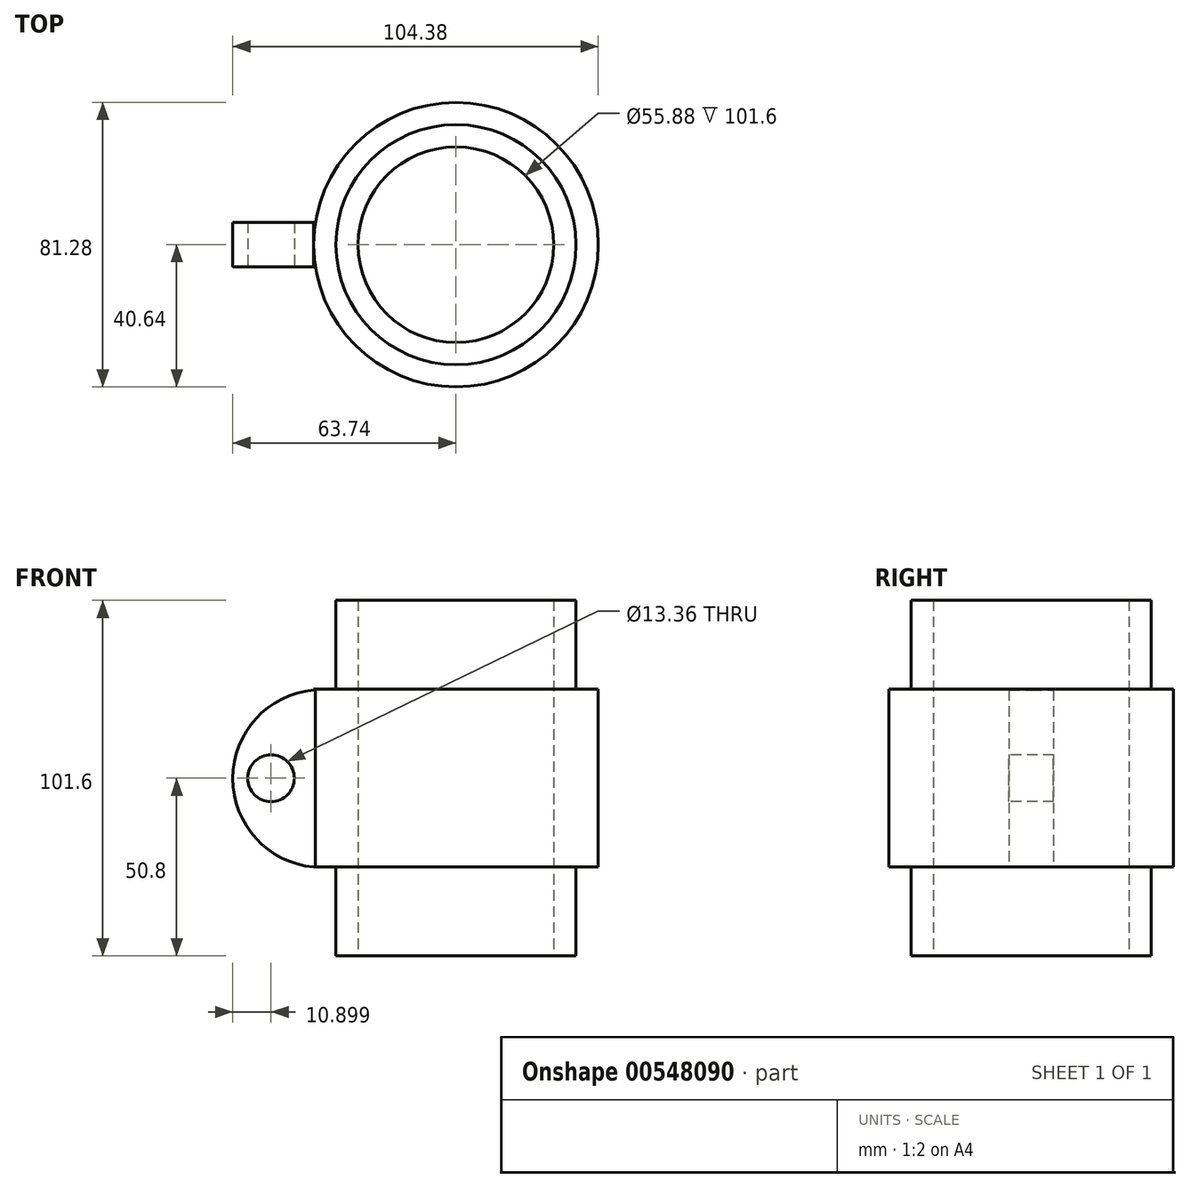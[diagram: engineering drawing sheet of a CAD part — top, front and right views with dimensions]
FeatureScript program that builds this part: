
annotation { "Feature Type Name" : "Feature", "Feature Type Description" : "" }
export const myFeature = defineFeature(function(context is Context, id is Id, definition is map)
    precondition{}
    {
        {
            var Q0;
            Q0=qCreatedBy(makeId("Front.planeOp"),FACE);
            var sketch = newSketch(context, id + "F0", { "sketchPlane" : qUnion([Q0])});
            skLineSegment(sketch, "E0.bottom", {"start": v(-27.94, 0) * mm, "end": v(-40.64, 0) * mm});
            skLineSegment(sketch, "E0.top", {"start": v(-27.94, 50.8) * mm, "end": v(-40.64, 50.8) * mm});
            skLineSegment(sketch, "E0.left", {"start": v(-27.94, 0) * mm, "end": v(-27.94, 50.8) * mm});
            skLineSegment(sketch, "E0.right", {"start": v(-40.64, 0) * mm, "end": v(-40.64, 50.8) * mm});
            skLineSegment(sketch, "E1", {"start": v(0, 0) * mm, "end": v(0, 38.6) * mm});
            skSolve(sketch);
        }
        {
            var Q0;
            Q0=makeQuery(id+"F0.imprint","IMPRINT",FACE,{"disambiguationData":[TD([[makeQuery(id+"F0.imprint","IMPRINT",EDGE,{"derivedFrom":sQuery(id+"F0.wireOp",EDGE,"E0.bottom")}),-1.0]])]});
            var Q1;
            Q1=sQuery(id+"F0.wireOp",EDGE,"E1");
            revolve(context, id + "F1", {"entities" : qUnion([Q0]), "axis" : qUnion([Q1]), "revolveType" : RevolveType.FULL});
        }
        {
            var Q0;
            Q0=qCreatedBy(makeId("Front.planeOp"),FACE);
            var sketch = newSketch(context, id + "F2", { "sketchPlane" : qUnion([Q0])});
            skArc(sketch, "E2", {"start": v(-40.64, 50.6) * mm, "mid": v(-63.74, 25.3) * mm, "end": v(-40.64, 0) * mm});
            skLineSegment(sketch, "E3", {"start": v(-40.64, 50.6) * mm, "end": v(-40.64, 0) * mm});
            skLineSegment(sketch, "E4.bottom", {"start": v(-40.64, 50.6) * mm, "end": v(-35.56, 50.6) * mm});
            skLineSegment(sketch, "E4.top", {"start": v(-40.64, 0) * mm, "end": v(-35.56, 0) * mm});
            skLineSegment(sketch, "E4.right", {"start": v(-35.56, 50.6) * mm, "end": v(-35.56, 0) * mm});
            skSolve(sketch);
        }
        {
            var Q0;
            Q0 = qSketchRegion(id + "F2", true);
            extrude(context, id + "F3", {"entities" : qUnion([Q0]), "operationType" : NewBodyOperationType.ADD, "depth" : 6.35 * mm, "offsetDistance" : 25.4 * mm, "hasSecondDirection" : true, "secondDirectionOppositeDirection" : true, "secondDirectionDepth" : 6.35 * mm});
        }
        {
            var Q0;
            Q0=makeQuery(id+"F3.opExtrude","CAP_FACE",FACE,{"disambiguationData":[OSD([sQuery(id+"F2.wireOp",EDGE,"E2"),sQuery(id+"F2.wireOp",EDGE,"E4.bottom"),sQuery(id+"F2.wireOp",EDGE,"E4.top"),sQuery(id+"F2.wireOp",EDGE,"E4.right")])],"isStart":false});
            var sketch = newSketch(context, id + "F4", { "sketchPlane" : qUnion([Q0])});
            skCircle(sketch, "E5", {"center": v(-52.84, 25.4) * mm, "radius": 6.68 * mm});
            skSolve(sketch);
        }
        {
            var Q0;
            Q0=makeQuery(id+"F4.imprint","IMPRINT",FACE,{"disambiguationData":[TD([[makeQuery(id+"F4.imprint","IMPRINT",EDGE,{"derivedFrom":sQuery(id+"F4.wireOp",EDGE,"E5")}),1.0]])]});
            extrude(context, id + "F5", {"entities" : qUnion([Q0]), "operationType" : NewBodyOperationType.REMOVE, "oppositeDirection" : true, "depth" : 25.4 * mm, "offsetDistance" : 25.4 * mm});
        }
        {
            var Q0;
            Q0=qCreatedBy(makeId("Front.planeOp"),FACE);
            var sketch = newSketch(context, id + "F6", { "sketchPlane" : qUnion([Q0])});
            skLineSegment(sketch, "E6", {"start": v(0, 0) * mm, "end": v(0, 69.09) * mm});
            skSolve(sketch);
        }
        {
            var Q0;
            Q0=qCreatedBy(makeId("Front.planeOp"),FACE);
            var sketch = newSketch(context, id + "F7", { "sketchPlane" : qUnion([Q0])});
            skLineSegment(sketch, "E7.bottom", {"start": v(-27.94, 76.2) * mm, "end": v(-34.3, 76.2) * mm});
            skLineSegment(sketch, "E7.top", {"start": v(-27.94, -25.4) * mm, "end": v(-34.3, -25.4) * mm});
            skLineSegment(sketch, "E7.left", {"start": v(-27.94, 76.2) * mm, "end": v(-27.94, -25.4) * mm});
            skLineSegment(sketch, "E7.right", {"start": v(-34.3, 76.2) * mm, "end": v(-34.3, -25.4) * mm});
            skLineSegment(sketch, "E8", {"start": v(0, 0) * mm, "end": v(0, 147.64) * mm});
            skSolve(sketch);
        }
        {
            var Q0;
            Q0=makeQuery(id+"F7.imprint","IMPRINT",FACE,{"disambiguationData":[TD([[makeQuery(id+"F7.imprint","IMPRINT",EDGE,{"derivedFrom":sQuery(id+"F7.wireOp",EDGE,"E7.bottom")}),1.0]])]});
            var Q1;
            Q1=sQuery(id+"F7.wireOp",EDGE,"E8");
            revolve(context, id + "F8", {"operationType" : NewBodyOperationType.ADD, "entities" : qUnion([Q0]), "axis" : qUnion([Q1]), "revolveType" : RevolveType.FULL});
        }
    });
